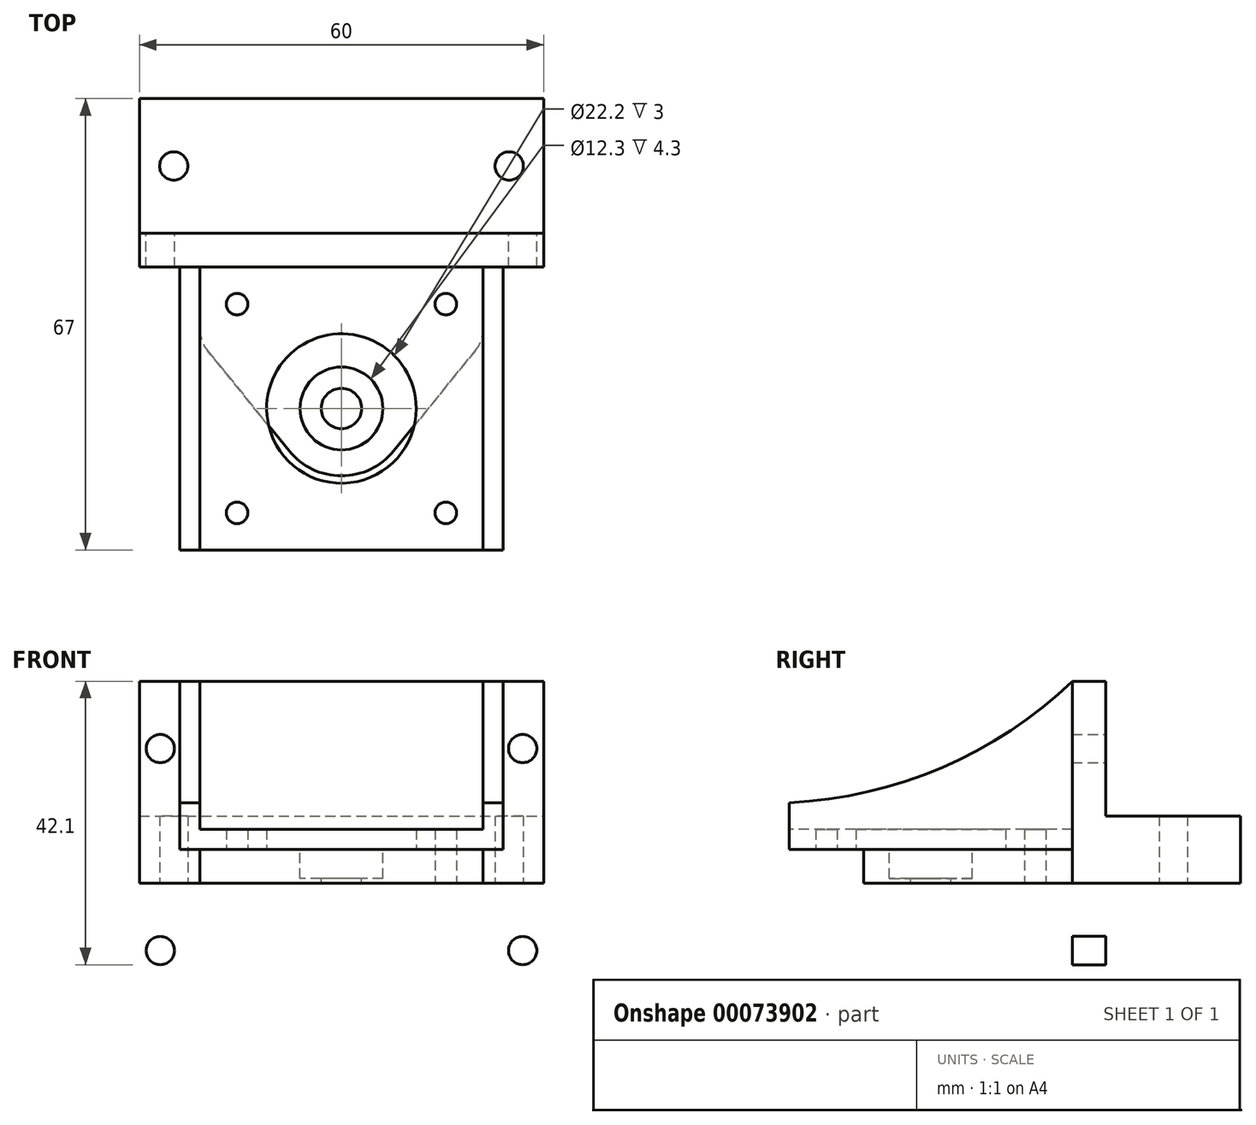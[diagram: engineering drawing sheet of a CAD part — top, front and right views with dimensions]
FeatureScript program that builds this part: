
annotation { "Feature Type Name" : "Feature", "Feature Type Description" : "" }
export const myFeature = defineFeature(function(context is Context, id is Id, definition is map)
    precondition{}
    {
        {
            var Q0;
            Q0=qCreatedBy(makeId("Top.planeOp"),FACE);
            var sketch = newSketch(context, id + "F0", { "sketchPlane" : qUnion([Q0])});
            skLineSegment(sketch, "E0.bottom", {"start": v(-30, 0) * mm, "end": v(30, 0) * mm});
            skLineSegment(sketch, "E0.top", {"start": v(-30, -20) * mm, "end": v(30, -20) * mm});
            skLineSegment(sketch, "E0.left", {"start": v(-30, 0) * mm, "end": v(-30, -20) * mm});
            skLineSegment(sketch, "E0.right", {"start": v(30, 0) * mm, "end": v(30, -20) * mm});
            skCircle(sketch, "E1", {"center": v(-24.9, -10) * mm, "radius": 2.1 * mm});
            skPoint(sketch, "E1.centerSnap0", {"position": v(-30, -10) * mm});
            skCircle(sketch, "E2.MirrorC", {"center": v(24.9, -10) * mm, "radius": 2.1 * mm});
            skLineSegment(sketch, "E3", {"start": v(-30, -20) * mm, "end": v(-30, -25) * mm});
            skLineSegment(sketch, "E4", {"start": v(-30, -25) * mm, "end": v(30, -25) * mm});
            skLineSegment(sketch, "E5", {"start": v(30, -25) * mm, "end": v(30, -20) * mm});
            skLineSegment(sketch, "E6.bottom", {"start": v(-21, -67) * mm, "end": v(21, -67) * mm});
            skCircle(sketch, "E7", {"center": v(-15.5, -30.5) * mm, "radius": 1.6 * mm});
            skCircle(sketch, "E8.MirrorC", {"center": v(15.5, -30.5) * mm, "radius": 1.6 * mm});
            skCircle(sketch, "E9", {"center": v(-15.5, -61.5) * mm, "radius": 1.6 * mm});
            skCircle(sketch, "E10.MirrorC", {"center": v(15.5, -61.5) * mm, "radius": 1.6 * mm});
            skLineSegment(sketch, "E11", {"start": v(15.5, -28.9) * mm, "end": v(15.5, -25) * mm, "construction": true});
            skLineSegment(sketch, "E12", {"start": v(15.5, -63.1) * mm, "end": v(15.5, -67) * mm, "construction": true});
            skLineSegment(sketch, "E13", {"start": v(-17.1, -30.5) * mm, "end": v(-21, -30.5) * mm, "construction": true});
            skLineSegment(sketch, "E14", {"start": v(-21, -25) * mm, "end": v(-21, -67) * mm});
            skLineSegment(sketch, "E15.MirrorCS", {"start": v(21, -25) * mm, "end": v(21, -67) * mm});
            skLineSegment(sketch, "E16", {"start": v(17.1, -30.5) * mm, "end": v(21, -30.5) * mm, "construction": true});
            skLineSegment(sketch, "E17", {"start": v(17.1, -61.5) * mm, "end": v(21, -61.5) * mm, "construction": true});
            skLineSegment(sketch, "E18.0", {"start": v(-24, -25) * mm, "end": v(-24, -67) * mm});
            skLineSegment(sketch, "E19.MirrorCS", {"start": v(24, -25) * mm, "end": v(24, -67) * mm});
            skLineSegment(sketch, "E20.0", {"start": v(-21, -70) * mm, "end": v(21, -70) * mm});
            skLineSegment(sketch, "E21", {"start": v(-24, -67) * mm, "end": v(-21, -70) * mm});
            skLineSegment(sketch, "E22", {"start": v(24, -67) * mm, "end": v(21, -70) * mm});
            skLineSegment(sketch, "E23", {"start": v(0, -67) * mm, "end": v(0, -25) * mm, "construction": true});
            skLineSegment(sketch, "E24", {"start": v(-21, -46) * mm, "end": v(21, -46) * mm, "construction": true});
            skCircle(sketch, "E25", {"center": v(0, -46) * mm, "radius": 11.1 * mm});
            skSolve(sketch);
        }
        {
            var Q0;
            Q0=makeQuery(id+"F0.imprint","IMPRINT",FACE,{"disambiguationData":[TD([[makeQuery(id+"F0.imprint","IMPRINT",EDGE,{"derivedFrom":sQuery(id+"F0.wireOp",EDGE,"E0.bottom")}),-1.0]])]});
            extrude(context, id + "F1", {"entities" : qUnion([Q0]), "depth" : 5 * mm});
        }
        {
            var Q0;
            Q0=makeQuery(id+"F1.opExtrude","SWEPT_FACE",FACE,{"disambiguationData":[OSD([sQuery(id+"F0.wireOp",EDGE,"E0.top")])]});
            var sketch = newSketch(context, id + "F2", { "sketchPlane" : qUnion([Q0])});
            skLineSegment(sketch, "E26.bottom", {"start": v(-30, 25) * mm, "end": v(30, 25) * mm});
            skLineSegment(sketch, "E26.top", {"start": v(-30, 5) * mm, "end": v(30, 5) * mm});
            skLineSegment(sketch, "E26.left", {"start": v(-30, 25) * mm, "end": v(-30, 5) * mm});
            skLineSegment(sketch, "E26.right", {"start": v(30, 25) * mm, "end": v(30, 5) * mm});
            skCircle(sketch, "E27", {"center": v(-26.9, 15) * mm, "radius": 2.1 * mm});
            skPoint(sketch, "E27.centerSnap0", {"position": v(-30, 15) * mm});
            skCircle(sketch, "E28.MirrorC", {"center": v(26.9, 15) * mm, "radius": 2.1 * mm});
            skLineSegment(sketch, "E29.0", {"start": v(-30, 5) * mm, "end": v(-30, 0) * mm});
            skLineSegment(sketch, "E29.1", {"start": v(-30, 0) * mm, "end": v(30, 0) * mm});
            skLineSegment(sketch, "E29.2", {"start": v(30, 5) * mm, "end": v(30, 0) * mm});
            skSolve(sketch);
        }
        {
            var Q0;
            Q0=makeQuery(id+"F2.imprint","IMPRINT",FACE,{"disambiguationData":[TD([[makeQuery(id+"F2.imprint","IMPRINT",EDGE,{"derivedFrom":sQuery(id+"F2.wireOp",EDGE,"E26.top")}),-1.0]])]});
            var Q1;
            Q1=makeQuery(id+"F2.imprint","IMPRINT",FACE,{"disambiguationData":[TD([[makeQuery(id+"F2.imprint","IMPRINT",EDGE,{"derivedFrom":sQuery(id+"F2.wireOp",EDGE,"E26.bottom")}),-1.0]])]});
            extrude(context, id + "F3", {"entities" : qUnion([Q0, Q1]), "operationType" : NewBodyOperationType.ADD, "depth" : 5 * mm});
        }
        {
            var Q0;
            Q0=makeQuery(id+"F0.imprint","IMPRINT",FACE,{"disambiguationData":[TD([[makeQuery(id+"F0.imprint","IMPRINT",EDGE,{"derivedFrom":sQuery(id+"F0.wireOp",EDGE,"E6.bottom")}),-1.0]])]});
            var Q1;
            Q1=makeQuery(id+"F3.opExtrude","SWEPT_FACE",FACE,{"disambiguationData":[OSD([sQuery(id+"F2.wireOp",EDGE,"E26.bottom")])]});
            extrude(context, id + "F4", {"entities" : qUnion([Q0]), "operationType" : NewBodyOperationType.ADD, "endBound" : BoundingType.UP_TO_SURFACE, "endBoundEntityFace" : qUnion([Q1]), "depth" : 25 * mm});
        }
        {
            var Q0;
            Q0=makeQuery(id+"F0.imprint","IMPRINT",FACE,{"disambiguationData":[TD([[makeQuery(id+"F0.imprint","IMPRINT",EDGE,{"derivedFrom":sQuery(id+"F0.wireOp",EDGE,"E6.bottom")}),1.0]])]});
            extrude(context, id + "F5", {"entities" : qUnion([Q0]), "operationType" : NewBodyOperationType.ADD, "depth" : 3 * mm});
        }
        {
            var Q0;
            Q0=makeQuery(id+"F4.opExtrude","SWEPT_FACE",FACE,{"disambiguationData":[OSD([sQuery(id+"F0.wireOp",EDGE,"E18.0")])]});
            var sketch = newSketch(context, id + "F6", { "sketchPlane" : qUnion([Q0])});
            skLineSegment(sketch, "E30.0", {"start": v(70, 25) * mm, "end": v(70, 0) * mm});
            skLineSegment(sketch, "E31", {"start": v(25, 0) * mm, "end": v(70, 0) * mm});
            skLineSegment(sketch, "E32", {"start": v(70, 0) * mm, "end": v(70, 6.9) * mm});
            skArc(sketch, "E33", {"start": v(25, 25) * mm, "mid": v(45.75, 11.6) * mm, "end": v(70, 6.9) * mm});
            skLineSegment(sketch, "E34.0", {"start": v(25, 25) * mm, "end": v(25, 0) * mm});
            skLineSegment(sketch, "E35.0", {"start": v(67, 25) * mm, "end": v(67, 0) * mm});
            skLineSegment(sketch, "E35.1", {"start": v(67, 25) * mm, "end": v(70, 25) * mm});
            skSolve(sketch);
        }
        {
            var Q0;
            {var subQ1=makeQuery(id+"F4.opExtrude","CAP_EDGE",EDGE,{"disambiguationData":[OSD([sQuery(id+"F0.wireOp",EDGE,"E18.0")])],"isStart":false});Q0=makeQuery(id+"F6.imprint","IMPRINT",FACE,{"disambiguationData":[TD([[makeQuery(id+"F6.imprint","IMPRINT",EDGE,{"derivedFrom":subQ1}),-1.0]])]});}
            var Q1;
            {var subQ4=sQuery(id+"F6.wireOp",EDGE,"E30.0");Q1=makeQuery(id+"F6.imprint","IMPRINT",FACE,{"disambiguationData":[TD([[makeQuery(id+"F6.imprint","IMPRINT",EDGE,{"derivedFrom":subQ4}),-1.0]])]});}
            extrude(context, id + "F7", {"entities" : qUnion([Q0, Q1]), "operationType" : NewBodyOperationType.REMOVE, "endBound" : BoundingType.THROUGH_ALL, "oppositeDirection" : true, "depth" : 25 * mm});
        }
        {
            var Q0;
            Q0=makeQuery(id+"F0.imprint","IMPRINT",FACE,{"disambiguationData":[TD([[makeQuery(id+"F0.imprint","IMPRINT",EDGE,{"derivedFrom":sQuery(id+"F0.wireOp",EDGE,"E0.bottom")}),-1.0]])]});
            extrude(context, id + "F8", {"entities" : qUnion([Q0]), "oppositeDirection" : true, "depth" : 5 * mm});
        }
        {
            var Q0;
            Q0=makeQuery(id+"F0.imprint","IMPRINT",FACE,{"disambiguationData":[TD([[makeQuery(id+"F0.imprint","IMPRINT",EDGE,{"derivedFrom":sQuery(id+"F0.wireOp",EDGE,"E6.bottom")}),1.0]])]});
            var sketch = newSketch(context, id + "F9", { "sketchPlane" : qUnion([Q0])});
            skPoint(sketch, "E36.0", {"position": v(0, -46) * mm});
            skCircle(sketch, "E37", {"center": v(0, -46) * mm, "radius": 6.15 * mm});
            skLineSegment(sketch, "E38", {"start": v(30, -25) * mm, "end": v(7.75, -52.31) * mm});
            skLineSegment(sketch, "E39", {"start": v(-30, -25) * mm, "end": v(-7.75, -52.31) * mm});
            skArc(sketch, "E40", {"start": v(-7.75, -52.31) * mm, "mid": v(0, -56) * mm, "end": v(7.75, -52.31) * mm});
            skLineSegment(sketch, "E41.0", {"start": v(30, 0) * mm, "end": v(30, -25) * mm});
            skLineSegment(sketch, "E41.1", {"start": v(-30, 0) * mm, "end": v(-30, -25) * mm});
            skLineSegment(sketch, "E42.0", {"start": v(-30, -20) * mm, "end": v(30, -20) * mm});
            skLineSegment(sketch, "E43", {"start": v(30, -25) * mm, "end": v(-30, -25) * mm});
            skCircle(sketch, "E44", {"center": v(0, -46) * mm, "radius": 3 * mm});
            skSolve(sketch);
        }
        {
            var Q0;
            {var subQ7=sQuery(id+"F9.wireOp",EDGE,"E42.0");Q0=makeQuery(id+"F9.imprint","IMPRINT",FACE,{"disambiguationData":[TD([[makeQuery(id+"F9.imprint","IMPRINT",EDGE,{"derivedFrom":subQ7}),-1.0]])]});}
            extrude(context, id + "F10", {"entities" : qUnion([Q0]), "operationType" : NewBodyOperationType.ADD, "oppositeDirection" : true, "depth" : 25 * mm});
        }
        {
            var Q0;
            Q0=makeQuery(id+"F9.imprint","IMPRINT",FACE,{"disambiguationData":[TD([[makeQuery(id+"F9.imprint","IMPRINT",EDGE,{"derivedFrom":makeQuery(id+"F0.imprint","IMPRINT",EDGE,{"derivedFrom":sQuery(id+"F0.wireOp",EDGE,"E7")})}),-1.0]])]});
            var Q1;
            {var subQ10=sQuery(id+"F9.wireOp",EDGE,"f1a987d3-3d6a-4107-b72d-43f94a35c171.0");Q1=makeQuery(id+"F9.imprint","IMPRINT",FACE,{"disambiguationData":[TD([[makeQuery(id+"F9.imprint","IMPRINT",EDGE,{"derivedFrom":subQ10}),-1.0]])]});}
            var Q2;
            Q2=makeQuery(id+"F9.imprint","IMPRINT",FACE,{"disambiguationData":[TD([[makeQuery(id+"F9.imprint","IMPRINT",EDGE,{"derivedFrom":sQuery(id+"F9.wireOp",EDGE,"E37")}),1.0]])]});
            var Q3;
            Q3=makeQuery(id+"F9.imprint","IMPRINT",FACE,{"disambiguationData":[TD([[makeQuery(id+"F9.imprint","IMPRINT",EDGE,{"derivedFrom":sQuery(id+"F9.wireOp",EDGE,"E37")}),-1.0]])]});
            var Q4;
            Q4=makeQuery(id+"F9.imprint","IMPRINT",FACE,{"disambiguationData":[TD([[makeQuery(id+"F9.imprint","IMPRINT",EDGE,{"derivedFrom":makeQuery(id+"F0.imprint","IMPRINT",EDGE,{"derivedFrom":sQuery(id+"F0.wireOp",EDGE,"E7")})}),1.0]])]});
            var Q5;
            Q5=makeQuery(id+"F9.imprint","IMPRINT",FACE,{"disambiguationData":[TD([[makeQuery(id+"F9.imprint","IMPRINT",EDGE,{"derivedFrom":makeQuery(id+"F0.imprint","IMPRINT",EDGE,{"derivedFrom":sQuery(id+"F0.wireOp",EDGE,"E8.MirrorC")})}),-1.0]])]});
            var Q6;
            Q6=makeQuery(id+"F10.opExtrude","CAP_FACE",FACE,{"disambiguationData":[OSD([sQuery(id+"F9.wireOp",EDGE,"E41.0"),sQuery(id+"F9.wireOp",EDGE,"E41.1"),sQuery(id+"F9.wireOp",EDGE,"E42.0"),sQuery(id+"F9.wireOp",EDGE,"E43")])],"isStart":false});
            extrude(context, id + "F11", {"entities" : qUnion([Q0, Q1, Q2, Q3, Q4, Q5]), "operationType" : NewBodyOperationType.ADD, "endBound" : BoundingType.UP_TO_SURFACE, "oppositeDirection" : true, "endBoundEntityFace" : qUnion([Q6]), "depth" : 5.5 * mm});
        }
        {
            var Q0;
            Q0=makeQuery(id+"F9.imprint","IMPRINT",FACE,{"disambiguationData":[TD([[makeQuery(id+"F9.imprint","IMPRINT",EDGE,{"derivedFrom":sQuery(id+"F9.wireOp",EDGE,"E44")}),1.0]])]});
            var Q1;
            Q1=sQuery(id+"F9.wireOp",EDGE,"E37");
            extrude(context, id + "F12", {"entities" : qUnion([Q0]), "operationType" : NewBodyOperationType.REMOVE, "surfaceEntities" : qUnion([Q1]), "endBound" : BoundingType.THROUGH_ALL, "oppositeDirection" : true, "depth" : 4 * mm});
        }
        {
            var Q0;
            Q0=makeQuery(id+"F10.opExtrude","SWEPT_FACE",FACE,{"disambiguationData":[OSD([sQuery(id+"F9.wireOp",EDGE,"E42.0")])]});
            var sketch = newSketch(context, id + "F13", { "sketchPlane" : qUnion([Q0])});
            skCircle(sketch, "E45.0", {"center": v(26.9, 15) * mm, "radius": 2.1 * mm, "construction": true});
            skCircle(sketch, "E45.1", {"center": v(-26.9, 15) * mm, "radius": 2.1 * mm, "construction": true});
            skCircle(sketch, "E46.MirrorC", {"center": v(26.9, -15) * mm, "radius": 2.1 * mm});
            skCircle(sketch, "E47.MirrorC", {"center": v(-26.9, -15) * mm, "radius": 2.1 * mm});
            skSolve(sketch);
        }
        {
            var Q0;
            Q0=makeQuery(id+"F13.imprint","IMPRINT",FACE,{"disambiguationData":[TD([[makeQuery(id+"F13.imprint","IMPRINT",EDGE,{"derivedFrom":sQuery(id+"F13.wireOp",EDGE,"E46.MirrorC")}),-1.0]])]});
            var Q1;
            Q1=makeQuery(id+"F13.imprint","IMPRINT",FACE,{"disambiguationData":[TD([[makeQuery(id+"F13.imprint","IMPRINT",EDGE,{"derivedFrom":sQuery(id+"F13.wireOp",EDGE,"E47.MirrorC")}),-1.0]])]});
            extrude(context, id + "F14", {"entities" : qUnion([Q0, Q1]), "operationType" : NewBodyOperationType.REMOVE, "endBound" : BoundingType.THROUGH_ALL, "oppositeDirection" : true, "depth" : 25 * mm});
        }
        {
            var Q0;
            Q0=makeQuery(id+"F11.opExtrude","SWEPT_FACE",FACE,{"disambiguationData":[OSD([sQuery(id+"F0.wireOp",EDGE,"E14")])]});
            var sketch = newSketch(context, id + "F15", { "sketchPlane" : qUnion([Q0])});
            skLineSegment(sketch, "E48.0", {"start": v(25, -25) * mm, "end": v(25, 0) * mm});
            skLineSegment(sketch, "E48.1", {"start": v(52.31, 0) * mm, "end": v(56, 0) * mm});
            skLineSegment(sketch, "E48.2", {"start": v(25, 0) * mm, "end": v(52.31, 0) * mm});
            skLineSegment(sketch, "E49", {"start": v(56, 0) * mm, "end": v(56, -5.5) * mm});
            skArc(sketch, "E50", {"start": v(56, -5.5) * mm, "mid": v(38.65, -12.3) * mm, "end": v(25, -25) * mm});
            skLineSegment(sketch, "E51", {"start": v(56, -5.5) * mm, "end": v(56, -25) * mm});
            skPoint(sketch, "E51.endSnap0", {"position": v(30.53, -25) * mm});
            skLineSegment(sketch, "E52", {"start": v(56, -25) * mm, "end": v(25, -25) * mm});
            skSolve(sketch);
        }
        {
            var Q0;
            {var subQ5=sQuery(id+"F15.wireOp",EDGE,"E51");Q0=makeQuery(id+"F15.imprint","IMPRINT",FACE,{"disambiguationData":[TD([[makeQuery(id+"F15.imprint","IMPRINT",EDGE,{"derivedFrom":subQ5}),-1.0]])]});}
            var Q1;
            {var subQ1=sQuery(id+"F15.wireOp",EDGE,"E50");var subQ3=sQuery(id+"F15.wireOp",EDGE,"E52");var subQ5=makeQuery(id+"F15.imprint","INTERSECT",VERTEX,{"derivedFrom":[sQuery(id+"F15.wireOp",EDGE,"E48.0"),subQ1,subQ3]});Q1=makeQuery(id+"F15.imprint","IMPRINT",FACE,{"disambiguationData":[TD([[makeQuery(id+"F15.imprint","IMPRINT",EDGE,{"disambiguationData":[TD([[subQ5,1.0]])],"derivedFrom":subQ1}),1.0]])]});}
            extrude(context, id + "F16", {"entities" : qUnion([Q0, Q1]), "operationType" : NewBodyOperationType.REMOVE, "endBound" : BoundingType.THROUGH_ALL, "oppositeDirection" : true, "depth" : 25 * mm});
        }
        {
            var Q0;
            Q0=makeQuery(id+"F11.opExtrude","SWEPT_EDGE",EDGE,{"disambiguationData":[OSD([sQuery(id+"F0.wireOp",EDGE,"E15.MirrorCS"),sQuery(id+"F9.wireOp",EDGE,"E38")])]});
            var Q1;
            Q1=makeQuery(id+"F11.opExtrude","SWEPT_EDGE",EDGE,{"disambiguationData":[OSD([sQuery(id+"F0.wireOp",EDGE,"E14"),sQuery(id+"F9.wireOp",EDGE,"E39")])]});
            var Q2;
            Q2=makeQuery(id+"F16.boolean.opBoolean","INTERSECT",EDGE,{"derivedFrom":[makeQuery(id+"F11.opExtrude","SWEPT_FACE",FACE,{"disambiguationData":[OSD([sQuery(id+"F9.wireOp",EDGE,"E38")])]}),makeQuery(id+"F16.opExtrude","SWEPT_FACE",FACE,{"disambiguationData":[OSD([sQuery(id+"F15.wireOp",EDGE,"E50")])]})]});
            fillet(context, id + "F17", {"entities" : qUnion([Q0, Q1, Q2]), "radius" : 5 * mm, "tangentPropagation" : true, "allowEdgeOverflow" : false});
        }
        {
            var Q0;
            Q0=makeQuery(id+"F9.imprint","IMPRINT",FACE,{"disambiguationData":[TD([[makeQuery(id+"F9.imprint","IMPRINT",EDGE,{"derivedFrom":sQuery(id+"F9.wireOp",EDGE,"E37")}),1.0]])]});
            extrude(context, id + "F18", {"entities" : qUnion([Q0]), "operationType" : NewBodyOperationType.REMOVE, "oppositeDirection" : true, "depth" : 4.3 * mm});
        }
    });
